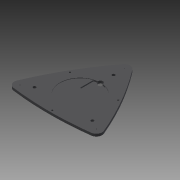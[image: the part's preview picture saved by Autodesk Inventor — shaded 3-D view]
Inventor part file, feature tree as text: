
AUTODESK INVENTOR PART (.ipt)
format: ipt  version: 2013 (Build 170138000, 138)  size: 194,048 bytes
history: native  units: mm
features: extrude x9, sketch x9, projected_geometry x4, fillet x1, pattern_circular x1
ambient origin geometry x8: Origin, YZ Plane, XZ Plane, XY Plane, X Axis, Y Axis, Z Axis, Center Point
feature tree (24):
  extrude  "Extrusion2"  Depth=250.0mm
  extrude  "Extrusion3"  Depth=8.5mm
  extrude  "Extrusion4"  Depth=60.325mm
  extrude  "Extrusion5"  Depth=3.175mm
  fillet  "Fillet1"  Radius=12.5mm
  extrude  "Extrusion9"  Depth=1.905mm TaperAngle=0.0deg
  extrude  "Extrusion10"  Depth=62.5mm
  pattern_circular  "Circular Pattern1"  [2 undecoded]
  extrude  "Extrusion6"  Depth=558.8mm TaperAngle=0.0deg
  extrude  "Extrusion7"  Depth=12.7mm TaperAngle=0.0deg
  extrude  "Extrusion8"  Depth=12.7mm TaperAngle=0.0deg
  sketch  "Sketch1"  dims[d0=300.0mm d1=250.0mm]
  sketch  "Sketch2"  dims[d2=3.175mm d3=8.5mm]
  sketch  "Sketch3"  dims[d4=50.0mm d5=60.325mm]
  sketch  "Sketch4"  dims[d6=25.0mm d9=3.175mm d10=12.5mm d11=0.0mm]
  sketch  "Sketch5"  dims[d12=210.0mm d14=1.905mm d15=0.0mm]
  sketch  "Sketch6"  dims[d16=75.0mm d18=62.5mm]
  projected_geometry  "Projected Loop1"
  projected_geometry  "Projected Loop2"
  projected_geometry  "Projected Loop3"
  sketch  "Sketch7"  dims[d19=5.715mm d20=0.0mm]
  projected_geometry  "Projected Loop4"
  sketch  "Sketch8"  dims[d21=25.0mm]
  sketch  "Sketch9"  dims[d23=5.715mm d24=0.0mm d25=3.175mm d26=558.8mm d27=101.6mm d28=0.0mm d29=0.0mm d30=12.7mm d31=0.0mm d32=12.7mm d33=0.0mm d34=23.0mm d36=7.9375mm d37=0.0mm d38=15.0mm d40=0.28125mm d41=0.0mm d42=30.0mm d43=360.0deg]
note: 2 required parameter values undecoded (feature->parameter linkage not recoverable at this tier; creation-order binding heuristic only, values carry confidence <= 0.55)
